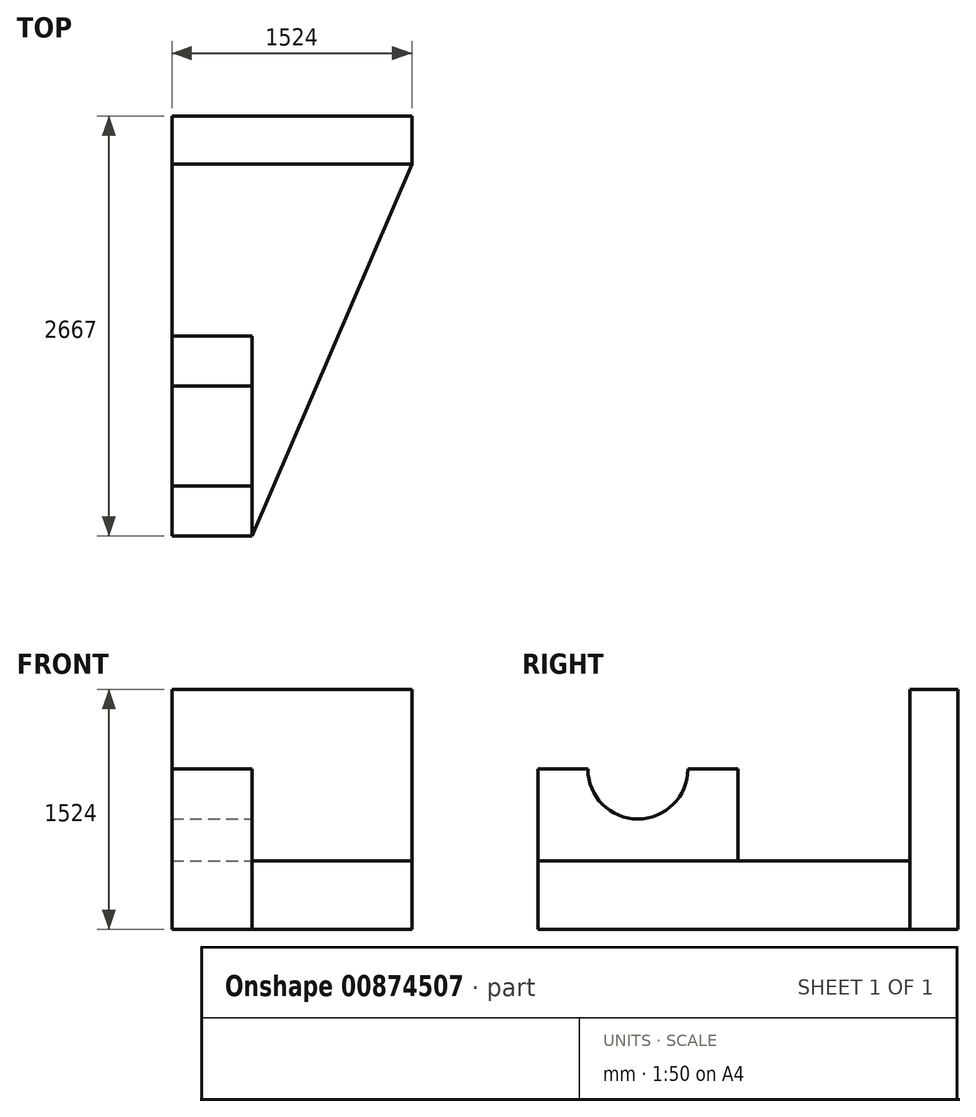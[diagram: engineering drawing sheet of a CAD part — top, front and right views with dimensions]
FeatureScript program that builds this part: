
annotation { "Feature Type Name" : "Feature", "Feature Type Description" : "" }
export const myFeature = defineFeature(function(context is Context, id is Id, definition is map)
    precondition{}
    {
        {
            var Q0;
            Q0=qCreatedBy(makeId("Front.planeOp"),FACE);
            var sketch = newSketch(context, id + "F0", { "sketchPlane" : qUnion([Q0])});
            skLineSegment(sketch, "E0.bottom", {"start": v(0, 0) * mm, "end": v(-1524, 0) * mm});
            skLineSegment(sketch, "E0.top", {"start": v(0, 1524) * mm, "end": v(-1524, 1524) * mm});
            skLineSegment(sketch, "E0.left", {"start": v(0, 0) * mm, "end": v(0, 1524) * mm});
            skLineSegment(sketch, "E0.right", {"start": v(-1524, 0) * mm, "end": v(-1524, 1524) * mm});
            skSolve(sketch);
        }
        {
            var Q0;
            Q0=qSketchRegion(id+"F0",true);
            extrude(context, id + "F1", {"entities" : qUnion([Q0]), "depth" : 304.8 * mm, "offsetDistance" : 25.4 * mm});
        }
        {
            var Q0;
            Q0=makeQuery(id+"F1.opExtrude","CAP_FACE",FACE,{"disambiguationData":[OSD([sQuery(id+"F0.wireOp",EDGE,"E0.bottom"),sQuery(id+"F0.wireOp",EDGE,"E0.top"),sQuery(id+"F0.wireOp",EDGE,"E0.left"),sQuery(id+"F0.wireOp",EDGE,"E0.right")])],"isStart":false});
            var sketch = newSketch(context, id + "F2", { "sketchPlane" : qUnion([Q0])});
            skLineSegment(sketch, "E1.bottom", {"start": v(-1524, 0) * mm, "end": v(0, 0) * mm});
            skLineSegment(sketch, "E1.top", {"start": v(-1524, 434.05) * mm, "end": v(0, 434.05) * mm});
            skLineSegment(sketch, "E1.left", {"start": v(-1524, 0) * mm, "end": v(-1524, 434.05) * mm});
            skLineSegment(sketch, "E1.right", {"start": v(0, 0) * mm, "end": v(0, 434.05) * mm});
            skSolve(sketch);
        }
        {
            var Q0;
            Q0=makeQuery(id+"F2.imprint","IMPRINT",FACE,{"disambiguationData":[TD([[makeQuery(id+"F2.imprint","IMPRINT",EDGE,{"derivedFrom":sQuery(id+"F2.wireOp",EDGE,"E1.bottom")}),-1.0]])]});
            extrude(context, id + "F3", {"entities" : qUnion([Q0]), "operationType" : NewBodyOperationType.ADD, "depth" : 2362.2 * mm, "offsetDistance" : 25.4 * mm});
        }
        {
            var Q0;
            Q0=makeQuery(id+"F3.opExtrude","SWEPT_FACE",FACE,{"disambiguationData":[OSD([sQuery(id+"F2.wireOp",EDGE,"E1.top")])]});
            var sketch = newSketch(context, id + "F4", { "sketchPlane" : qUnion([Q0])});
            skLineSegment(sketch, "E2.bottom", {"start": v(-1524, -2667) * mm, "end": v(-1016, -2667) * mm});
            skLineSegment(sketch, "E2.top", {"start": v(-1524, -1397) * mm, "end": v(-1016, -1397) * mm});
            skLineSegment(sketch, "E2.left", {"start": v(-1524, -2667) * mm, "end": v(-1524, -1397) * mm});
            skLineSegment(sketch, "E2.right", {"start": v(-1016, -2667) * mm, "end": v(-1016, -1397) * mm});
            skSolve(sketch);
        }
        {
            var Q0;
            Q0=makeQuery(id+"F4.imprint","IMPRINT",FACE,{"disambiguationData":[TD([[makeQuery(id+"F4.imprint","IMPRINT",EDGE,{"derivedFrom":sQuery(id+"F4.wireOp",EDGE,"E2.bottom")}),1.0]])]});
            extrude(context, id + "F5", {"entities" : qUnion([Q0]), "operationType" : NewBodyOperationType.ADD, "depth" : 584.2 * mm, "offsetDistance" : 25.4 * mm});
        }
        {
            var Q0;
            Q0=makeQuery(id+"F5.opExtrude","SWEPT_FACE",FACE,{"disambiguationData":[OSD([sQuery(id+"F4.wireOp",EDGE,"E2.right")])]});
            var sketch = newSketch(context, id + "F6", { "sketchPlane" : qUnion([Q0])});
            skCircle(sketch, "E3", {"center": v(-2032, 1018.25) * mm, "radius": 634.68 * mm});
            skSolve(sketch);
        }
        {
            var Q0;
            {var subQ0=sQuery(id+"F6.wireOp",EDGE,"E3");var subQ1=makeQuery(id+"F5.opExtrude","CAP_EDGE",EDGE,{"disambiguationData":[OSD([sQuery(id+"F4.wireOp",EDGE,"E2.right")])],"isStart":true});var subQ2=makeQuery(id+"F6.imprint","INTERSECT",VERTEX,{"disambiguationData":[OD(0.0)],"derivedFrom":[subQ1,subQ0]});Q0=makeQuery(id+"F6.imprint","IMPRINT",FACE,{"disambiguationData":[TD([[makeQuery(id+"F6.imprint","IMPRINT",EDGE,{"disambiguationData":[TD([[subQ2,-1.0]])],"derivedFrom":subQ0}),1.0]])]});}
            var Q1;
            {var subQ0=sQuery(id+"F6.wireOp",EDGE,"E3");var subQ1=makeQuery(id+"F5.opExtrude","CAP_EDGE",EDGE,{"disambiguationData":[OSD([sQuery(id+"F4.wireOp",EDGE,"E2.right")])],"isStart":false});var subQ2=makeQuery(id+"F6.imprint","INTERSECT",VERTEX,{"disambiguationData":[OD(0.0)],"derivedFrom":[subQ1,subQ0]});Q1=makeQuery(id+"F6.imprint","IMPRINT",FACE,{"disambiguationData":[TD([[makeQuery(id+"F6.imprint","IMPRINT",EDGE,{"disambiguationData":[TD([[subQ2,1.0]])],"derivedFrom":subQ0}),1.0]])]});}
            extrude(context, id + "F7", {"entities" : qUnion([Q0, Q1]), "operationType" : NewBodyOperationType.ADD, "oppositeDirection" : true, "depth" : 508 * mm, "offsetDistance" : 25.4 * mm});
        }
        {
            var Q0;
            {var subQ0=sQuery(id+"F6.wireOp",EDGE,"E3");var subQ1=sQuery(id+"F4.wireOp",EDGE,"E2.right");var subQ2=makeQuery(id+"F5.opExtrude","CAP_EDGE",EDGE,{"disambiguationData":[OSD([subQ1])],"isStart":false});var subQ3=makeQuery(id+"F6.imprint","INTERSECT",VERTEX,{"disambiguationData":[OD(0.0)],"derivedFrom":[subQ2,subQ0]});Q0=makeQuery(id+"F7.boolean.opBoolean","MERGE",FACE,{"derivedFrom":[makeQuery(id+"F5.opExtrude","SWEPT_FACE",FACE,{"disambiguationData":[OSD([subQ1])]}),makeQuery(id+"F7.opExtrude","CAP_FACE",FACE,{"disambiguationData":[OSD([subQ1,subQ0]),TDD([makeQuery(id+"F6.imprint","IMPRINT",EDGE,{"disambiguationData":[TD([[subQ3,1.0]])],"derivedFrom":subQ0}),makeQuery(id+"F6.imprint","IMPRINT",EDGE,{"disambiguationData":[TD([[subQ3,-1.0]])],"derivedFrom":subQ2})])],"isStart":true})]});}
            var sketch = newSketch(context, id + "F8", { "sketchPlane" : qUnion([Q0])});
            skLineSegment(sketch, "E4", {"start": v(-2667, 434.05) * mm, "end": v(-1397, 434.05) * mm});
            skLineSegment(sketch, "E5", {"start": v(-1397, 434.05) * mm, "end": v(-2032, 434.05) * mm});
            skLineSegment(sketch, "E6", {"start": v(-2032, 434.05) * mm, "end": v(-2032, 1652.93) * mm});
            skLineSegment(sketch, "E7", {"start": v(-2032, 1652.93) * mm, "end": v(-2666.68, 1018.25) * mm});
            skLineSegment(sketch, "E8", {"start": v(-2666.68, 1018.25) * mm, "end": v(-1397, 1018.25) * mm});
            skLineSegment(sketch, "E9", {"start": v(-1397, 1018.25) * mm, "end": v(-2032, 1652.93) * mm});
            skCircle(sketch, "E10", {"center": v(-2031.84, 1018.25) * mm, "radius": 317.5 * mm});
            skSolve(sketch);
        }
        {
            var Q0;
            {var subQ0=sQuery(id+"F8.wireOp",EDGE,"E8");var subQ1=sQuery(id+"F8.wireOp",EDGE,"E6");var subQ2=makeQuery(id+"F8.imprint","INTERSECT",VERTEX,{"derivedFrom":[subQ1,subQ0]});Q0=makeQuery(id+"F8.imprint","IMPRINT",FACE,{"disambiguationData":[TD([[makeQuery(id+"F8.imprint","IMPRINT",EDGE,{"disambiguationData":[TD([[subQ2,-1.0]])],"derivedFrom":subQ1}),1.0]])]});}
            var Q1;
            {var subQ0=sQuery(id+"F8.wireOp",EDGE,"E8");var subQ1=sQuery(id+"F8.wireOp",EDGE,"E6");var subQ2=makeQuery(id+"F8.imprint","INTERSECT",VERTEX,{"derivedFrom":[subQ1,subQ0]});Q1=makeQuery(id+"F8.imprint","IMPRINT",FACE,{"disambiguationData":[TD([[makeQuery(id+"F8.imprint","IMPRINT",EDGE,{"disambiguationData":[TD([[subQ2,-1.0]])],"derivedFrom":subQ1}),-1.0]])]});}
            var Q2;
            {var subQ0=sQuery(id+"F8.wireOp",EDGE,"E10");var subQ1=sQuery(id+"F8.wireOp",EDGE,"E6");var subQ2=makeQuery(id+"F8.imprint","INTERSECT",VERTEX,{"disambiguationData":[OD(0.0)],"derivedFrom":[subQ1,subQ0]});Q2=makeQuery(id+"F8.imprint","IMPRINT",FACE,{"disambiguationData":[TD([[makeQuery(id+"F8.imprint","IMPRINT",EDGE,{"disambiguationData":[TD([[subQ2,-1.0]])],"derivedFrom":subQ1}),1.0]])]});}
            var Q3;
            {var subQ0=sQuery(id+"F8.wireOp",EDGE,"E10");var subQ1=sQuery(id+"F8.wireOp",EDGE,"E6");var subQ2=makeQuery(id+"F8.imprint","INTERSECT",VERTEX,{"disambiguationData":[OD(0.0)],"derivedFrom":[subQ1,subQ0]});Q3=makeQuery(id+"F8.imprint","IMPRINT",FACE,{"disambiguationData":[TD([[makeQuery(id+"F8.imprint","IMPRINT",EDGE,{"disambiguationData":[TD([[subQ2,-1.0]])],"derivedFrom":subQ1}),-1.0]])]});}
            extrude(context, id + "F9", {"entities" : qUnion([Q0, Q1, Q2, Q3]), "operationType" : NewBodyOperationType.REMOVE, "oppositeDirection" : true, "depth" : 2413 * mm, "offsetDistance" : 25.4 * mm});
        }
        {
            var Q0;
            Q0=makeQuery(id+"F3.opExtrude","SWEPT_FACE",FACE,{"disambiguationData":[OSD([sQuery(id+"F2.wireOp",EDGE,"E1.top")])]});
            var sketch = newSketch(context, id + "F10", { "sketchPlane" : qUnion([Q0])});
            skLineSegment(sketch, "E11", {"start": v(-1016, -2667) * mm, "end": v(0, -304.8) * mm});
            skSolve(sketch);
        }
        {
            var Q0;
            Q0=makeQuery(id+"F10.imprint","IMPRINT",FACE,{"disambiguationData":[TD([[makeQuery(id+"F10.imprint","IMPRINT",EDGE,{"derivedFrom":sQuery(id+"F10.wireOp",EDGE,"E11")}),-1.0]])]});
            extrude(context, id + "F11", {"entities" : qUnion([Q0]), "operationType" : NewBodyOperationType.REMOVE, "oppositeDirection" : true, "depth" : 1445.26 * mm, "offsetDistance" : 25.4 * mm});
        }
    });
